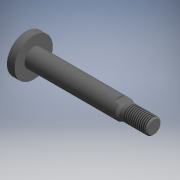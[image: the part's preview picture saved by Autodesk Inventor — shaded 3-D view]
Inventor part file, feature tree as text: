
AUTODESK INVENTOR PART (.ipt)
format: ipt  version: 2017.3 (Build 213256000, 256)  size: 122,368 bytes
history: native  units: mm (DEFAULTED — no unit token found)
features: other x14, sketch x2, revolve x1, thread x1, extrude x1
ambient origin geometry x8: Origin, YZ Plane, XZ Plane, XY Plane, X Axis, Y Axis, Z Axis, Center Point
bodies: Solid1 (feature_tree)
feature tree (19):
  revolve  "Revolution1"  [1 undecoded]
  thread  "Thread1"  [1 undecoded]
  extrude  "Extrusion1"  [1 undecoded]
  other  "ROD_BODY_XY"
  other  "ROD_BODY_YZ"
  other  "ROD_BODY_ZX"
  other  "ROD_BODY_X"
  other  "ROD_BODY_Y"
  other  "ROD_BODY_Z"
  other  "ROD_BODY_Center"
  other  "ROD_NUT_XY"
  other  "ROD_NUT_YZ"
  other  "ROD_NUT_ZX"
  other  "ROD_NUT_X"
  other  "ROD_NUT_Y"
  other  "ROD_NUT_Z"
  other  "ROD_NUT_Center"
  sketch  "Sketch_3"  dims[d0=360.0deg d1=14.233mm d2=0.0mm d3=5.0mm d4=0.0mm]
  sketch  "Sketch_7"  dims[d5=0.0mm d6=0.0mm]
note: 3 required parameter values undecoded (feature->parameter linkage not recoverable at this tier; creation-order binding heuristic only, values carry confidence <= 0.55)